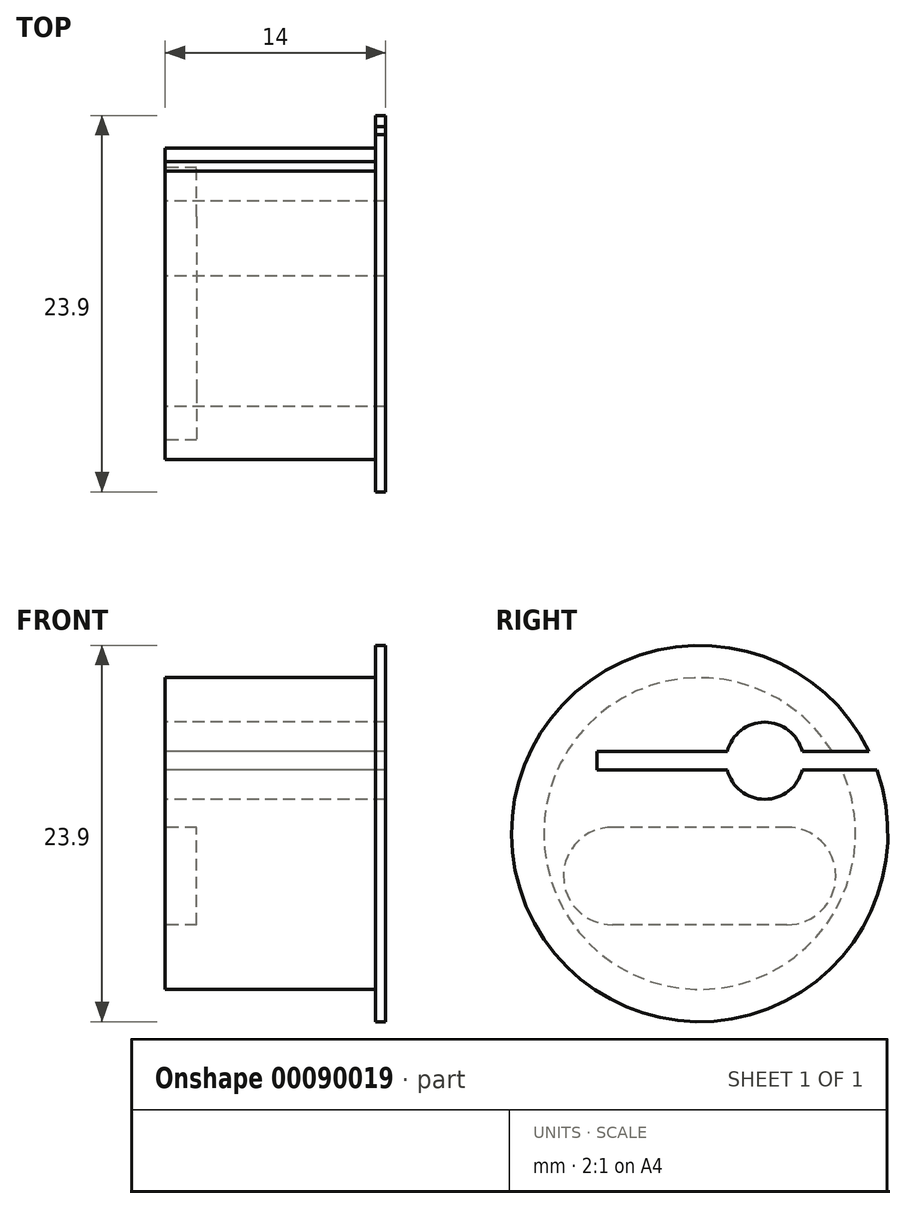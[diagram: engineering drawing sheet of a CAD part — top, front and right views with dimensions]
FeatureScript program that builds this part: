
annotation { "Feature Type Name" : "Feature", "Feature Type Description" : "" }
export const myFeature = defineFeature(function(context is Context, id is Id, definition is map)
    precondition{}
    {
        {
            var Q0;
            Q0=qCreatedBy(makeId("Front.planeOp"),FACE);
            var sketch = newSketch(context, id + "F0", { "sketchPlane" : qUnion([Q0])});
            skLineSegment(sketch, "E0", {"start": v(0, 0) * mm, "end": v(0, 11.95) * mm});
            skLineSegment(sketch, "E1", {"start": v(0, 11.95) * mm, "end": v(-0.65, 11.95) * mm});
            skLineSegment(sketch, "E2", {"start": v(-0.65, 11.95) * mm, "end": v(-0.65, 9.9) * mm});
            skLineSegment(sketch, "E3", {"start": v(-0.65, 9.9) * mm, "end": v(-14, 9.9) * mm});
            skLineSegment(sketch, "E4", {"start": v(-14, 9.9) * mm, "end": v(-14, 0) * mm});
            skLineSegment(sketch, "E5.MirrorCS", {"start": v(0, 0) * mm, "end": v(0, -11.95) * mm, "construction": true});
            skLineSegment(sketch, "E6.MirrorCS", {"start": v(-0.65, -11.95) * mm, "end": v(-0.65, -9.9) * mm, "construction": true});
            skLineSegment(sketch, "E7.MirrorCS", {"start": v(0, -11.95) * mm, "end": v(-0.65, -11.95) * mm, "construction": true});
            skLineSegment(sketch, "E8.MirrorCS", {"start": v(-14, -9.9) * mm, "end": v(-14, 0) * mm, "construction": true});
            skLineSegment(sketch, "E9.MirrorCS", {"start": v(-0.65, -9.9) * mm, "end": v(-14, -9.9) * mm, "construction": true});
            skLineSegment(sketch, "E10", {"start": v(-14, 0) * mm, "end": v(0, 0) * mm});
            skSolve(sketch);
        }
        {
            var Q0;
            Q0=qSketchRegion(id+"F0",true);
            var Q1;
            Q1=sQuery(id+"F0.wireOp",EDGE,"E10");
            revolve(context, id + "F1", {"entities" : qUnion([Q0]), "axis" : qUnion([Q1]), "revolveType" : RevolveType.FULL});
        }
        {
            var Q0;
            Q0=makeQuery(id+"F1.opRevolve","SWEPT_FACE",FACE,{"disambiguationData":[OSD([sQuery(id+"F0.wireOp",EDGE,"E4")])]});
            var sketch = newSketch(context, id + "F2", { "sketchPlane" : qUnion([Q0])});
            skArc(sketch, "E11", {"start": v(-1.75, 5.2) * mm, "mid": v(-4.13, 7.08) * mm, "end": v(-6.51, 5.2) * mm});
            skLineSegment(sketch, "E12.bottom", {"start": v(6.52, 4.05) * mm, "end": v(-1.75, 4.05) * mm});
            skLineSegment(sketch, "E12.top", {"start": v(6.52, 5.2) * mm, "end": v(-1.75, 5.2) * mm});
            skLineSegment(sketch, "E12.left", {"start": v(6.52, 4.05) * mm, "end": v(6.52, 5.2) * mm});
            skLineSegment(sketch, "E12.right", {"start": v(-11.24, 4.05) * mm, "end": v(-11.24, 5.2) * mm});
            skPoint(sketch, "E12.middle", {"position": v(-2.36, 4.62) * mm});
            skLineSegment(sketch, "E13", {"start": v(6.52, 4.63) * mm, "end": v(11.02, 4.63) * mm, "construction": true});
            skLineSegment(sketch, "E14.trimOffspring", {"start": v(-6.51, 5.2) * mm, "end": v(-11.24, 5.2) * mm});
            skLineSegment(sketch, "E15.trimOffspring", {"start": v(-6.51, 4.05) * mm, "end": v(-11.24, 4.05) * mm});
            skArc(sketch, "E16.trimOffspring", {"start": v(-6.51, 4.05) * mm, "mid": v(-4.13, 2.17) * mm, "end": v(-1.75, 4.05) * mm});
            skLineSegment(sketch, "E17", {"start": v(-1.75, 5.2) * mm, "end": v(-1.75, 4.05) * mm, "construction": true});
            skSolve(sketch);
        }
        {
            var Q0;
            Q0=qSketchRegion(id+"F2",true);
            extrude(context, id + "F3", {"entities" : qUnion([Q0]), "operationType" : NewBodyOperationType.REMOVE, "endBound" : BoundingType.THROUGH_ALL, "oppositeDirection" : true, "depth" : 25 * mm});
        }
        {
            var Q0;
            Q0=qSketchRegion(id+"F2",true);
            extrude(context, id + "F4", {"entities" : qUnion([Q0]), "operationType" : NewBodyOperationType.REMOVE, "endBound" : BoundingType.THROUGH_ALL, "oppositeDirection" : true, "depth" : 25 * mm});
        }
        {
            var Q0;
            Q0=makeQuery(id+"F1.opRevolve","SWEPT_FACE",FACE,{"disambiguationData":[OSD([sQuery(id+"F0.wireOp",EDGE,"E4")])]});
            var sketch = newSketch(context, id + "F5", { "sketchPlane" : qUnion([Q0])});
            skLineSegment(sketch, "E18.bottom", {"start": v(5.55, 0.4) * mm, "end": v(-5.55, 0.4) * mm});
            skLineSegment(sketch, "E18.top", {"start": v(5.55, -5.8) * mm, "end": v(-5.55, -5.8) * mm});
            skLineSegment(sketch, "E18.left", {"start": v(5.55, 0.4) * mm, "end": v(5.55, -5.8) * mm, "construction": true});
            skLineSegment(sketch, "E18.right", {"start": v(-5.55, 0.4) * mm, "end": v(-5.55, -5.8) * mm, "construction": true});
            skPoint(sketch, "E18.middle", {"position": v(0, -2.7) * mm});
            skArc(sketch, "E19", {"start": v(-5.55, 0.4) * mm, "mid": v(-8.65, -2.7) * mm, "end": v(-5.55, -5.8) * mm});
            skArc(sketch, "E20", {"start": v(5.55, -5.8) * mm, "mid": v(8.65, -2.7) * mm, "end": v(5.55, 0.4) * mm});
            skSolve(sketch);
        }
        {
            var Q0;
            Q0=qSketchRegion(id+"F5",true);
            extrude(context, id + "F6", {"entities" : qUnion([Q0]), "operationType" : NewBodyOperationType.REMOVE, "oppositeDirection" : true, "depth" : 2 * mm});
        }
        {
            var Q0;
            Q0=qSketchRegion(id+"F5",true);
            var Q1;
            Q1=makeQuery(id+"F6.boolean.opBoolean","COPY",FACE,{"derivedFrom":makeQuery(id+"F6.opExtrude","CAP_FACE",FACE,{"disambiguationData":[OSD([sQuery(id+"F5.wireOp",EDGE,"E18.bottom"),sQuery(id+"F5.wireOp",EDGE,"E18.top"),sQuery(id+"F5.wireOp",EDGE,"E19"),sQuery(id+"F5.wireOp",EDGE,"E20")])],"isStart":false})});
            extrude(context, id + "F7", {"entities" : qUnion([Q0]), "endBound" : BoundingType.UP_TO_SURFACE, "oppositeDirection" : true, "endBoundEntityFace" : qUnion([Q1]), "depth" : 25 * mm});
        }
    });
